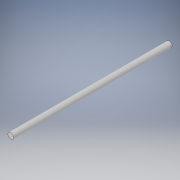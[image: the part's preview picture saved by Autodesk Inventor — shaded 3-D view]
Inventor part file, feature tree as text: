
AUTODESK INVENTOR PART (.ipt)
format: ipt  version: 2019 (Build 230136000, 136)  size: 90,624 bytes
history: native  units: mm
features: extrude x1, sketch x1
ambient origin geometry x8: Origin, YZ Plane, XZ Plane, XY Plane, X Axis, Y Axis, Z Axis, Center Point
bodies: Solid1 (feature_tree)
feature tree (2):
  extrude  "Extrusion1"  Depth=200.0mm TaperAngle=0.0deg
  sketch  "Sketch1"  dims[d0=7.0mm d1=200.0mm d2=0.0mm]
